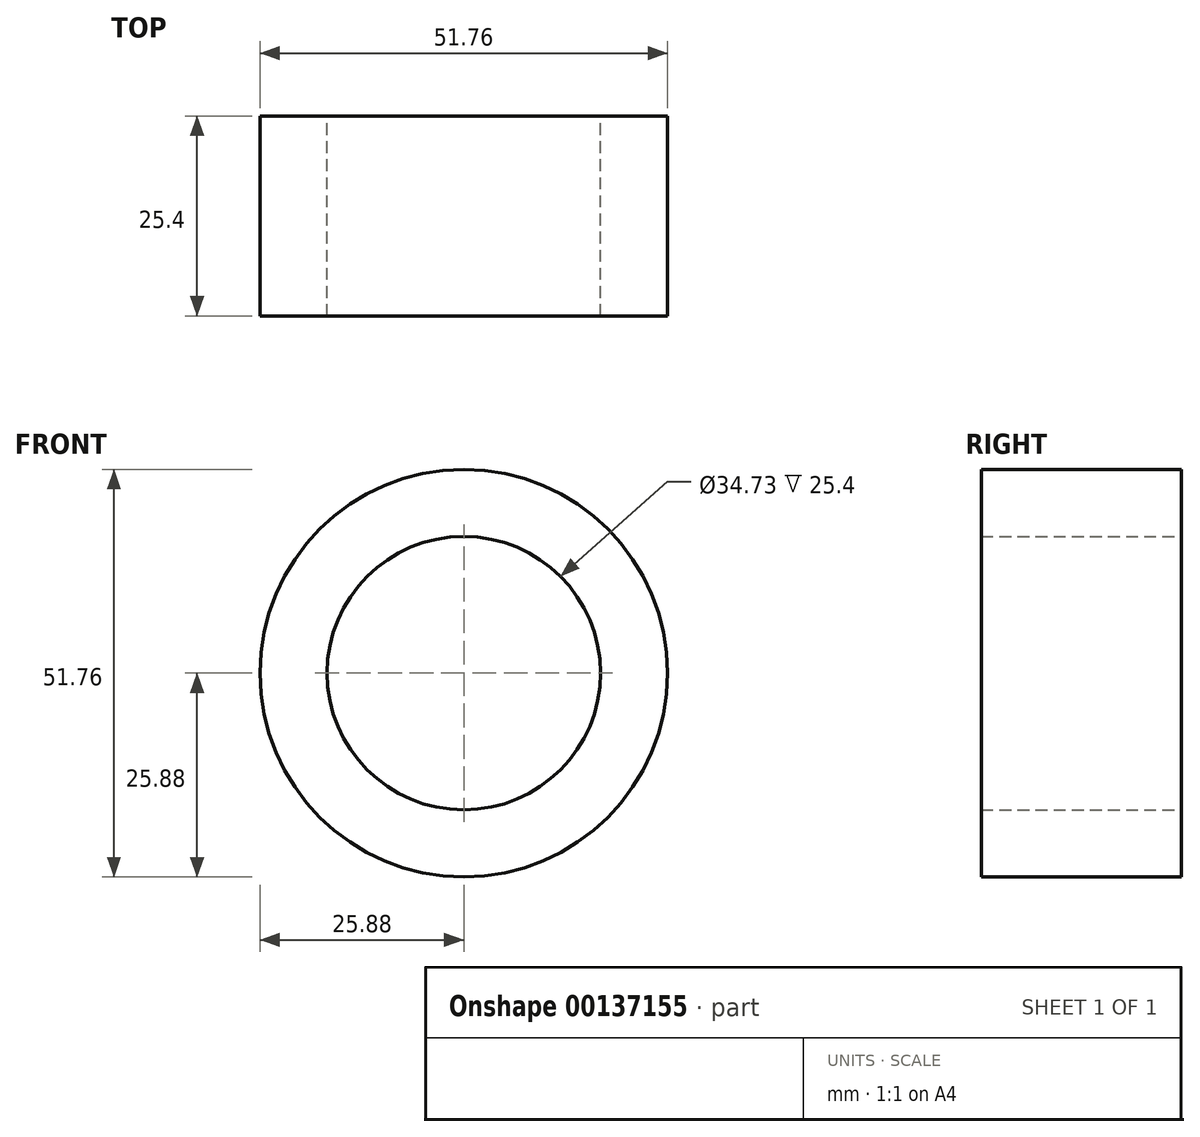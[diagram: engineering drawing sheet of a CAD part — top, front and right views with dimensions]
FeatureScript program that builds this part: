
annotation { "Feature Type Name" : "Feature", "Feature Type Description" : "" }
export const myFeature = defineFeature(function(context is Context, id is Id, definition is map)
    precondition{}
    {
        {
            var Q0;
            Q0=qCreatedBy(makeId("Front.planeOp"),FACE);
            var sketch = newSketch(context, id + "F0", { "sketchPlane" : qUnion([Q0])});
            skCircle(sketch, "E0", {"center": v(0, 0) * mm, "radius": 17.37 * mm});
            skCircle(sketch, "E1", {"center": v(0, 0) * mm, "radius": 25.88 * mm});
            skSolve(sketch);
        }
        {
            var Q0;
            Q0 = qSketchRegion(id + "F0", true);
            extrude(context, id + "F1", {"entities" : qUnion([Q0]), "depth" : 25.4 * mm});
        }
    });
